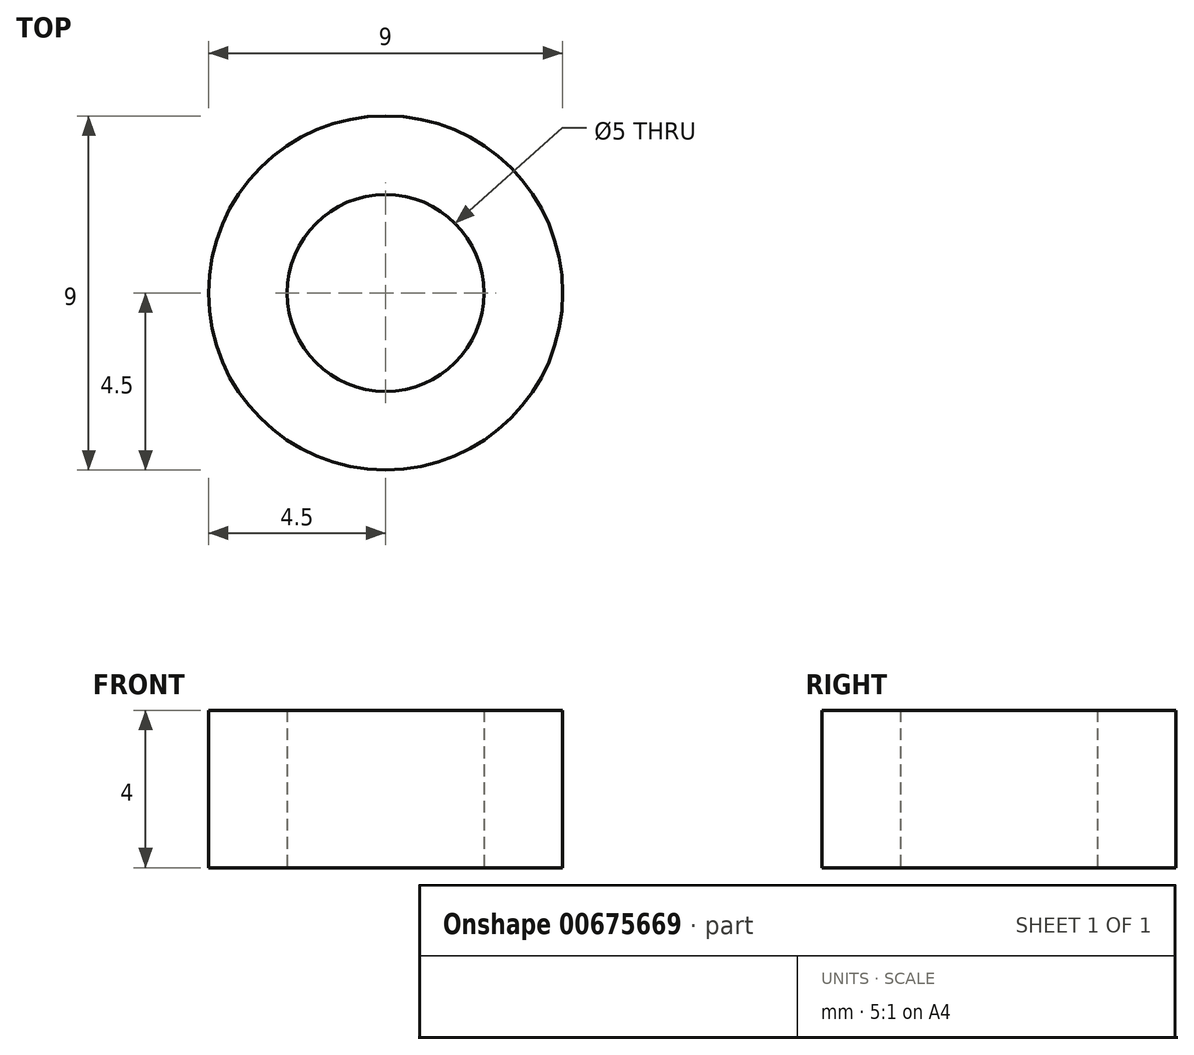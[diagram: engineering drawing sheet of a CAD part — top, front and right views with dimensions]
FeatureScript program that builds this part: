
annotation { "Feature Type Name" : "Feature", "Feature Type Description" : "" }
export const myFeature = defineFeature(function(context is Context, id is Id, definition is map)
    precondition{}
    {
        {
            var Q0;
            Q0=qCreatedBy(makeId("Top.planeOp"),FACE);
            var sketch = newSketch(context, id + "F0", { "sketchPlane" : qUnion([Q0])});
            skCircle(sketch, "E0", {"center": v(0, 0) * mm, "radius": 2.5 * mm});
            skCircle(sketch, "E1", {"center": v(0, 0) * mm, "radius": 4.5 * mm});
            skSolve(sketch);
        }
        {
            var Q0;
            Q0 = qSketchRegion(id + "F0", true);
            extrude(context, id + "F1", {"entities" : qUnion([Q0]), "depth" : 4 * mm, "offsetDistance" : 25 * mm});
        }
    });
